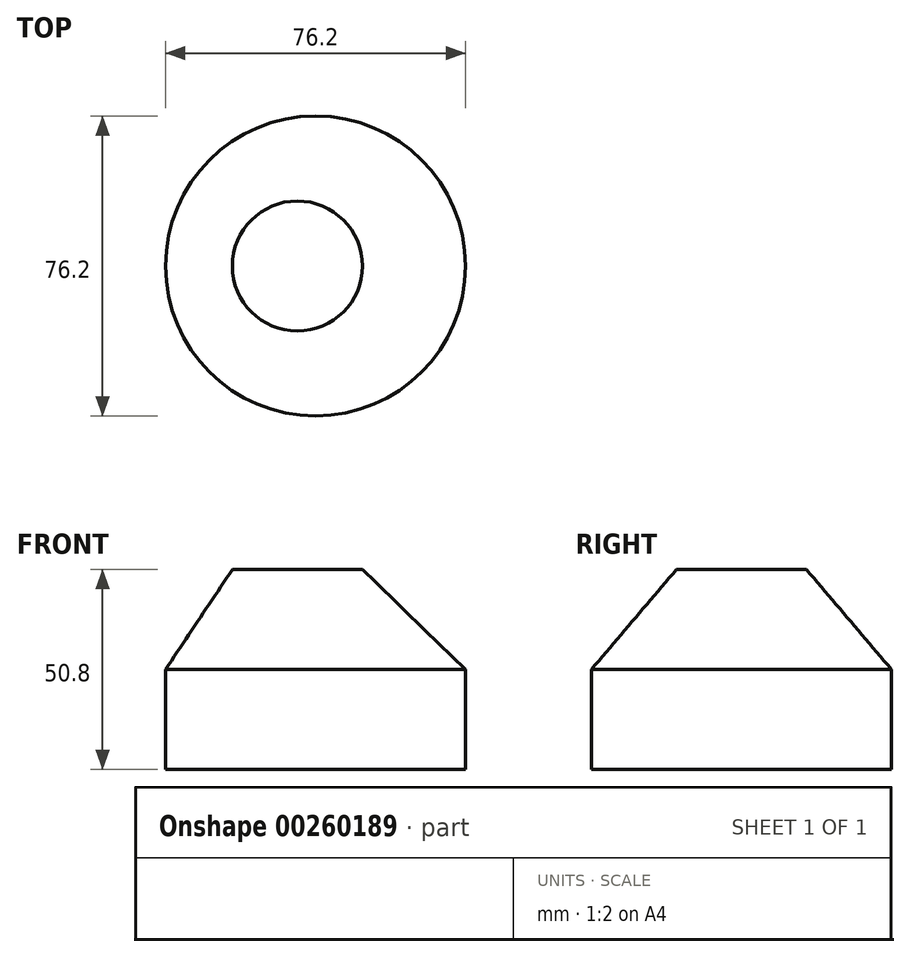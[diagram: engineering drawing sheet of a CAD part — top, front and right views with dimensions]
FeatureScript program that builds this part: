
annotation { "Feature Type Name" : "Feature", "Feature Type Description" : "" }
export const myFeature = defineFeature(function(context is Context, id is Id, definition is map)
    precondition{}
    {
        {
            var Q0;
            Q0=qCreatedBy(makeId("Top.planeOp"),FACE);
            var sketch = newSketch(context, id + "F0", { "sketchPlane" : qUnion([Q0])});
            skCircle(sketch, "E0", {"center": v(0, 0) * mm, "radius": 38.1 * mm});
            skSolve(sketch);
        }
        {
            var Q0;
            Q0=qCreatedBy(makeId("Top.planeOp"),FACE);
            var sketch = newSketch(context, id + "F1", { "sketchPlane" : qUnion([Q0])});
            skSolve(sketch);
        }
        {
            var Q0;
            Q0 = qSketchRegion(id + "F1", true);
            var Q1;
            Q1=makeQuery(id+"F0.imprint","IMPRINT",FACE,{"disambiguationData":[TD([[makeQuery(id+"F0.imprint","IMPRINT",EDGE,{"derivedFrom":sQuery(id+"F0.wireOp",EDGE,"E0")}),1.0]])]});
            extrude(context, id + "F2", {"entities" : qUnion([Q0, Q1]), "depth" : 25.4 * mm});
        }
        {
            var Q0;
            Q0=makeQuery(id+"F2.opExtrude","CAP_FACE",FACE,{"disambiguationData":[OSD([sQuery(id+"F0.wireOp",EDGE,"E0")])],"isStart":false});
            cPlane(context, id + "F3", {"entities" : qUnion([Q0]), "cplaneType" : CPlaneType.OFFSET, "offset" : 25.4 * mm, "width" : 152.4 * mm, "height" : 152.4 * mm});
        }
        {
            var Q0;
            Q0=qCreatedBy(id+"F3.planeOp",FACE);
            var sketch = newSketch(context, id + "F4", { "sketchPlane" : qUnion([Q0])});
            skCircle(sketch, "E1", {"center": v(-4.62, 0) * mm, "radius": 16.53 * mm});
            skSolve(sketch);
        }
        {
            var Q0;
            Q0=makeQuery(id+"F4.imprint","IMPRINT",FACE,{"disambiguationData":[TD([[makeQuery(id+"F4.imprint","IMPRINT",EDGE,{"derivedFrom":sQuery(id+"F4.wireOp",EDGE,"E1")}),1.0]])]});
            var Q1;
            Q1=makeQuery(id+"F2.opExtrude","CAP_FACE",FACE,{"disambiguationData":[OSD([sQuery(id+"F0.wireOp",EDGE,"E0")])],"isStart":false});
            loft(context, id + "F5", {"sheetProfilesArray" : [{ "sheetProfileEntities" : qUnion([Q0]) }, { "sheetProfileEntities" : qUnion([Q1]) }]});
        }
    });
